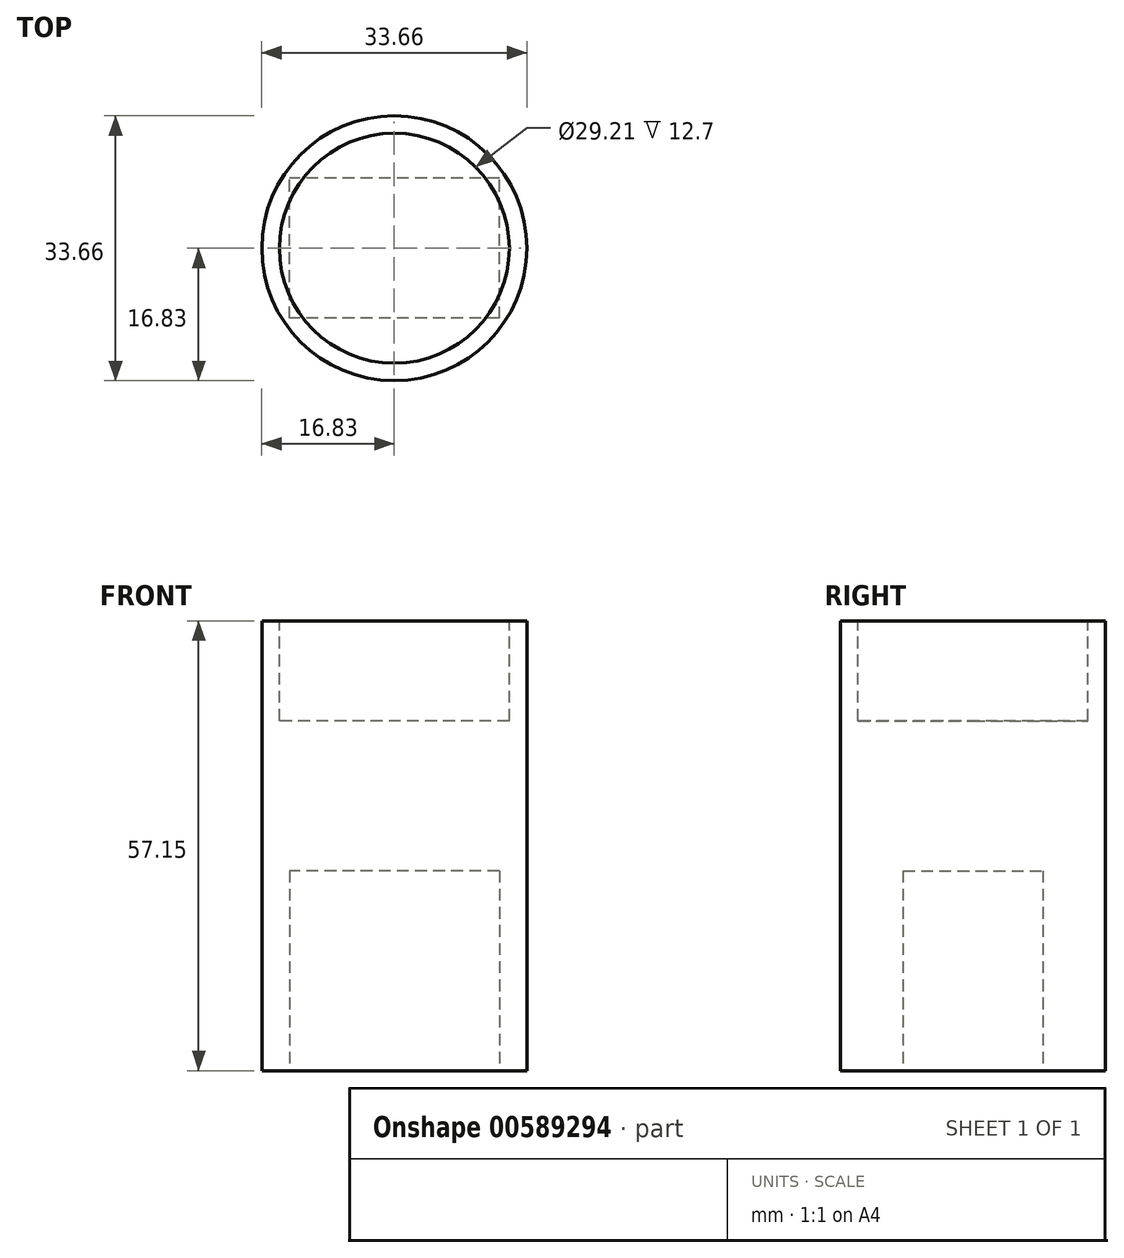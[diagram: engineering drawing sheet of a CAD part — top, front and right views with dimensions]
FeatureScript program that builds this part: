
annotation { "Feature Type Name" : "Feature", "Feature Type Description" : "" }
export const myFeature = defineFeature(function(context is Context, id is Id, definition is map)
    precondition{}
    {
        {
            var Q0;
            Q0=qCreatedBy(makeId("Top.planeOp"),FACE);
            var sketch = newSketch(context, id + "F0", { "sketchPlane" : qUnion([Q0])});
            skCircle(sketch, "E0", {"center": v(0, 0) * mm, "radius": 16.83 * mm});
            skSolve(sketch);
        }
        {
            var Q0;
            Q0=makeQuery(id+"F0.imprint","IMPRINT",FACE,{"disambiguationData":[TD([[makeQuery(id+"F0.imprint","IMPRINT",EDGE,{"derivedFrom":sQuery(id+"F0.wireOp",EDGE,"E0")}),1.0]])]});
            extrude(context, id + "F1", {"entities" : qUnion([Q0]), "depth" : 25.4 * mm, "offsetDistance" : 25.4 * mm, "hasSecondDirection" : true, "secondDirectionOppositeDirection" : true, "secondDirectionDepth" : 31.75 * mm});
        }
        {
            var Q0;
            Q0=makeQuery(id+"F1.opExtrude","CAP_FACE",FACE,{"disambiguationData":[OSD([sQuery(id+"F0.wireOp",EDGE,"E0")])],"isStart":false});
            cPlane(context, id + "F2", {"entities" : qUnion([Q0]), "cplaneType" : CPlaneType.OFFSET, "offset" : 0 * mm, "width" : 152.4 * mm, "height" : 152.4 * mm});
        }
        {
            var Q0;
            Q0=qCreatedBy(id+"F2.planeOp",FACE);
            var sketch = newSketch(context, id + "F3", { "sketchPlane" : qUnion([Q0])});
            skCircle(sketch, "E1", {"center": v(0, 0) * mm, "radius": 14.6 * mm});
            skSolve(sketch);
        }
        {
            var Q0;
            Q0 = qSketchRegion(id + "F3", true);
            extrude(context, id + "F4", {"entities" : qUnion([Q0]), "operationType" : NewBodyOperationType.REMOVE, "oppositeDirection" : true, "depth" : 12.7 * mm, "offsetDistance" : 25.4 * mm});
        }
        {
            var Q0;
            Q0=makeQuery(id+"F1.opExtrude","CAP_FACE",FACE,{"disambiguationData":[OSD([sQuery(id+"F0.wireOp",EDGE,"E0")])],"isStart":true});
            cPlane(context, id + "F5", {"entities" : qUnion([Q0]), "cplaneType" : CPlaneType.OFFSET, "offset" : 0 * mm, "width" : 152.4 * mm, "height" : 152.4 * mm});
        }
        {
            var Q0;
            Q0=qCreatedBy(id+"F5.planeOp",FACE);
            var sketch = newSketch(context, id + "F6", { "sketchPlane" : qUnion([Q0])});
            skLineSegment(sketch, "E2.bottom", {"start": v(13.33, 8.9) * mm, "end": v(-13.33, 8.9) * mm});
            skLineSegment(sketch, "E2.top", {"start": v(13.33, -8.9) * mm, "end": v(-13.33, -8.9) * mm});
            skLineSegment(sketch, "E2.left", {"start": v(13.34, 8.9) * mm, "end": v(13.34, -8.9) * mm});
            skLineSegment(sketch, "E2.right", {"start": v(-13.34, 8.9) * mm, "end": v(-13.33, -8.9) * mm});
            skPoint(sketch, "E2.middle", {"position": v(0, 0) * mm});
            skSolve(sketch);
        }
        {
            var Q0;
            Q0 = qSketchRegion(id + "F6", true);
            extrude(context, id + "F7", {"entities" : qUnion([Q0]), "operationType" : NewBodyOperationType.REMOVE, "oppositeDirection" : true, "depth" : 25.4 * mm, "offsetDistance" : 25.4 * mm});
        }
    });
